# Revit family: Crest Boiler FBD0751-2001
name_source: partatom
category: Mechanical Equipment
revit_build: Autodesk Revit 2015 (Build: 20140223_1515(x64)
units: mm (PartAtom-declared; Revit-internal decimal feet)

## types (6) — shared parameters
# of Electrical Connections = 1
A_WIDTH = 30"
Back Clearance = 24"
Description = CREST Duel Fuel Boiler
Drain Depth = 4"
FUEL TYPE = NATURAL/PROPANE GAS
Front Clearance = 30"
Fuel Type = Natural or LP
HEIGHT = 78"
Left Clearance = 24"
Manufacturer = Lochinvar
Right Clearance = 24"
Top Clearance = 24"
Voltage/Control = 24
Voltage/Heater = 120/1PH

## per-type parameters (varying)
- FBD0751: AIR INTAKE SIZE=6"; Air Intake Radius=3"; C_Depth to Vent=51"; D_Air Inlet Offset=13"; Depth=49"; Drain Offset=57"; E_Air Intake Offset=8 3/4"; F_Gas 1 Conn Height=23 3/4"; GALLON CAPACITY=73; GAS 1 CONN SIZE=1 1/4"; GAS 2 CONN SIZE=1 1/4"; G_Width to Gas 1=26 3/4"; Gas 1 Conn Radius=5/8"; Gas 2 Conn Height=9 3/8"; Gas 2 Conn Radius=5/8"; H_ Vent Offset=5 1/8"; INPUT RATE (BTUH)=750,000; J_Water Conn Offset=57 5/8"; K_Water Inlet Height=11 7/8"; L_Water Outlet Height=66 1/8"; SES BIM Studio #=17 0649 03; Total Amps=5; VENT SIZE=6"; Vent Radius=3"; WATER CONN SIZE=3"; Water Conn Radius=1 1/2"; Width to Gas 2=25 1/4"
- FBD1001: AIR INTAKE SIZE=6"; Air Intake Radius=3"; C_Depth to Vent=51"; D_Air Inlet Offset=13"; Depth=49"; Drain Offset=56 1/4"; E_Air Intake Offset=8 3/4"; F_Gas 1 Conn Height=23 1/8"; GALLON CAPACITY=77; GAS 1 CONN SIZE=1 1/4"; GAS 2 CONN SIZE=1 1/4"; G_Width to Gas 1=26 3/4"; Gas 1 Conn Radius=5/8"; Gas 2 Conn Height=4 3/4"; Gas 2 Conn Radius=5/8"; H_ Vent Offset=5 1/8"; INPUT RATE (BTUH)=1,000,000; J_Water Conn Offset=57 5/8"; K_Water Inlet Height=11 7/8"; L_Water Outlet Height=66 1/8"; SES BIM Studio #=2017 0649 03; Total Amps=6; VENT SIZE=6"; Vent Radius=3"; WATER CONN SIZE=3"; Water Conn Radius=1 1/2"; Width to Gas 2=16 1/2"
- FBD1251: AIR INTAKE SIZE=6"; Air Intake Radius=3"; C_Depth to Vent=51 3/8"; D_Air Inlet Offset=13"; Depth=49 3/8"; Drain Offset=61 7/8"; E_Air Intake Offset=8 3/4"; F_Gas 1 Conn Height=21 5/8"; GALLON CAPACITY=87; GAS 1 CONN SIZE=1 1/4"; GAS 2 CONN SIZE=1 1/4"; G_Width to Gas 1=26 3/4"; Gas 1 Conn Radius=5/8"; Gas 2 Conn Height=3"; Gas 2 Conn Radius=5/8"; H_ Vent Offset=6 1/2"; INPUT RATE (BTUH)=1,250,000; J_Water Conn Offset=57 3/4"; K_Water Inlet Height=11 7/8"; L_Water Outlet Height=66 1/8"; SES BIM Studio #=17 0649 03; Total Amps=7; VENT SIZE=8"; Vent Radius=4"; WATER CONN SIZE=3"; Water Conn Radius=1 1/2"; Width to Gas 2=15 3/4"
- FBD1501: AIR INTAKE SIZE=8"; Air Intake Radius=4"; C_Depth to Vent=62 3/8"; D_Air Inlet Offset=15 7/8"; Depth=60 3/8"; Drain Offset=61 7/8"; E_Air Intake Offset=9"; F_Gas 1 Conn Height=27 7/8"; GALLON CAPACITY=94; GAS 1 CONN SIZE=1 1/2"; GAS 2 CONN SIZE=1 1/2"; G_Width to Gas 1=26 7/8"; Gas 1 Conn Radius=3/4"; Gas 2 Conn Height=6 1/2"; Gas 2 Conn Radius=3/4"; H_ Vent Offset=5 1/8"; INPUT RATE (BTUH)=1,500,000; J_Water Conn Offset=68"; K_Water Inlet Height=12 3/8"; L_Water Outlet Height=65 3/8"; SES BIM Studio #=17 0649 03; Total Amps=10; VENT SIZE=8"; Vent Radius=4"; WATER CONN SIZE=4"; Water Conn Radius=2"; Width to Gas 2=25 1/4"
- FBD1751: AIR INTAKE SIZE=8"; Air Intake Radius=4"; C_Depth to Vent=61 1/2"; D_Air Inlet Offset=15 7/8"; Depth=59 1/2"; Drain Offset=61 7/8"; E_Air Intake Offset=9"; F_Gas 1 Conn Height=27 1/8"; GALLON CAPACITY=106; GAS 1 CONN SIZE=1 1/2"; GAS 2 CONN SIZE=1 1/2"; G_Width to Gas 1=27"; Gas 1 Conn Radius=3/4"; Gas 2 Conn Height=5 3/4"; Gas 2 Conn Radius=3/4"; H_ Vent Offset=5 1/8"; INPUT RATE (BTUH)=1,750,000; J_Water Conn Offset=68"; K_Water Inlet Height=12 3/8"; L_Water Outlet Height=65 3/8"; SES BIM Studio #=17 0649 03; Total Amps=10; VENT SIZE=8"; Vent Radius=4"; WATER CONN SIZE=4"; Water Conn Radius=2"; Width to Gas 2=25 1/4"
- FBD2001: AIR INTAKE SIZE=8"; Air Intake Radius=4"; C_Depth to Vent=61 1/2"; D_Air Inlet Offset=15 7/8"; Depth=59 1/2"; Drain Offset=61 7/8"; E_Air Intake Offset=9"; F_Gas 1 Conn Height=26 3/4"; GALLON CAPACITY=111; GAS 1 CONN SIZE=1 1/2"; GAS 2 CONN SIZE=1 1/2"; G_Width to Gas 1=27"; Gas 1 Conn Radius=3/4"; Gas 2 Conn Height=7 7/8"; Gas 2 Conn Radius=3/4"; H_ Vent Offset=5 1/8"; INPUT RATE (BTUH)=2,000,000; J_Water Conn Offset=68"; K_Water Inlet Height=12 3/8"; L_Water Outlet Height=65 3/8"; SES BIM Studio #=17 0649 03; Total Amps=13; VENT SIZE=8"; Vent Radius=4"; WATER CONN SIZE=4"; Water Conn Radius=2"; Width to Gas 2=25 1/4"

note: column(s) folded — value = type name in every type: MODEL NO., Model

## geometry (parser evidence)
native form markers: Sweep x2
no freeform markers — native parametric forms only
